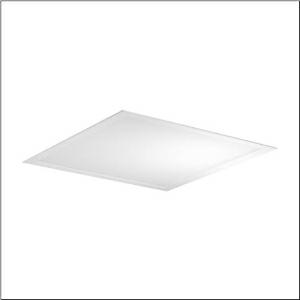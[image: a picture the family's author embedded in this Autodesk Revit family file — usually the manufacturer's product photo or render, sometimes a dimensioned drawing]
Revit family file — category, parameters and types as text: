
# Revit family: apollon_21_square_51mq11w72313
name_source: partatom
category: Lighting Fixtures
units: mm (PartAtom-declared; Revit-internal decimal feet)

## family parameters
Cut with Voids When Loaded = No
Host = Face
Light Source = No
Part Type = Normal
Room Calculation Point = No
Round Connector Dimension = Use Diameter
Shared = No

## types (1)
- Apollon 21 square (1 x LED, 4000 lm, 33 W, 3000K)
    Apparent Load = 33 VA
    CIE Flux Codes = 61 87 97 100 100
    Color Rendering = 80
    Color Temperature = 3000K
    Default Elevation = 1800 mm
    Description = Apollon 21 square, office luminaire, primary optical cover: micro prismatic cover, of PMMA, CAT 2 (L<= 3000cd/m²), light emission: direct distribution, primary light characteristic: symmetric, installation type: lay-in mounting, LED, rated luminous flux: 4.000lm, luminous efficacy: 121lm/W, light colour: 830, colour temperature: 3000K, control gear: ON/OFF, with terminal, 3-pole, mains connection: 220..240V, AC, 50/60Hz, rated input power: 33W, housing, of aluminium, traffic white (RAL 9016), module: M625, length: 620mm, width: 620mm, height: 40mm, housing upper side, of sheet steel, galvanised, protection rating (complete): IP20, protection rating (lamp compartment, on room side): IP50, insulation class (complete): insulation class II (safety insulation), certification: CE, ENEC, permissible operating ambient temperature: -20..+40°C, packaging unit: 1 piece
    Height = 0 mm  [stored 0 ft]
    Lamp = 1 x LED
    Lamp Light Flux = 4000 lm
    Lamp Power = 33 W
    Lamp count = 1
    Length = 620 mm
    Luminous efficacy = 121 lm/W
    Manufacturer = Siteco
    ModVariant = No
    Model = 51MQ11W72313
    Mounting Place = Ceiling
    Mounting Type = Recessed
    Number of Poles = 1
    OnlyDefault = Yes
    Power Factor = 1
    Product Name = Apollon 21 square
    Product group = office luminaire | ceiling recessed
    ProductGroupID = 400
    Protection Class = Protection class II
    Protection Degree = IP 20
    RLX_Detail_Level = 1
    RLX_Emergency_Light_Flux = 0 lm
    RLX_Emergency_Type = 0
    RLX_Emergency_Type_DB = No
    RlxData = <blob elided: 12881 chars, md5=6a402bd2>
    Socket = socket
    Standby Power = 0 W
    System Light Flux = 4000 lm
    System Power = 33 W
    Type Comments = Product without accessories
    Type Image = l_1291054.jpg
    URL = http://relux.com
    VarID = ---
    Voltage = 0 V
    Weight = 0.00 kg
    Width = 620 mm

note: [stored X ft] marks values corroborated as IEEE doubles in the binary element streams (Revit-internal decimal feet)

## geometry (parser evidence)
native form markers: Sweep x10
no freeform markers — native parametric forms only
